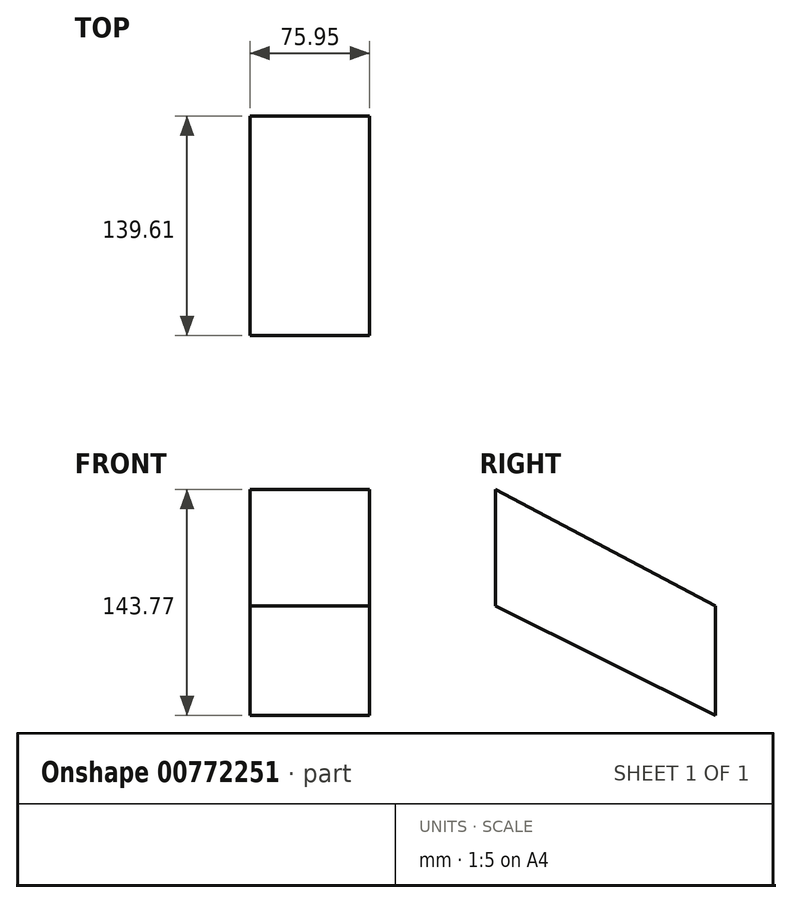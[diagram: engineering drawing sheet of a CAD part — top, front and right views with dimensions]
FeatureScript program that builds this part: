
annotation { "Feature Type Name" : "Feature", "Feature Type Description" : "" }
export const myFeature = defineFeature(function(context is Context, id is Id, definition is map)
    precondition{}
    {
        {
            var Q0;
            Q0=qCreatedBy(makeId("Right.planeOp"),FACE);
            var sketch = newSketch(context, id + "F0", { "sketchPlane" : qUnion([Q0])});
            skLineSegment(sketch, "E0", {"start": v(0, 74) * mm, "end": v(0, 0) * mm});
            skLineSegment(sketch, "E1", {"start": v(0, 0) * mm, "end": v(0, 74) * mm});
            skLineSegment(sketch, "E2", {"start": v(0, 74) * mm, "end": v(139.61, 0) * mm});
            skLineSegment(sketch, "E3", {"start": v(139.61, 0) * mm, "end": v(139.61, -69.76) * mm});
            skLineSegment(sketch, "E4", {"start": v(139.61, -69.76) * mm, "end": v(0, 0) * mm});
            skSolve(sketch);
        }
        {
            var Q0;
            Q0 = qSketchRegion(id + "F0", true);
            extrude(context, id + "F1", {"entities" : qUnion([Q0]), "depth" : 75.95 * mm, "offsetDistance" : 25.4 * mm});
        }
    });
